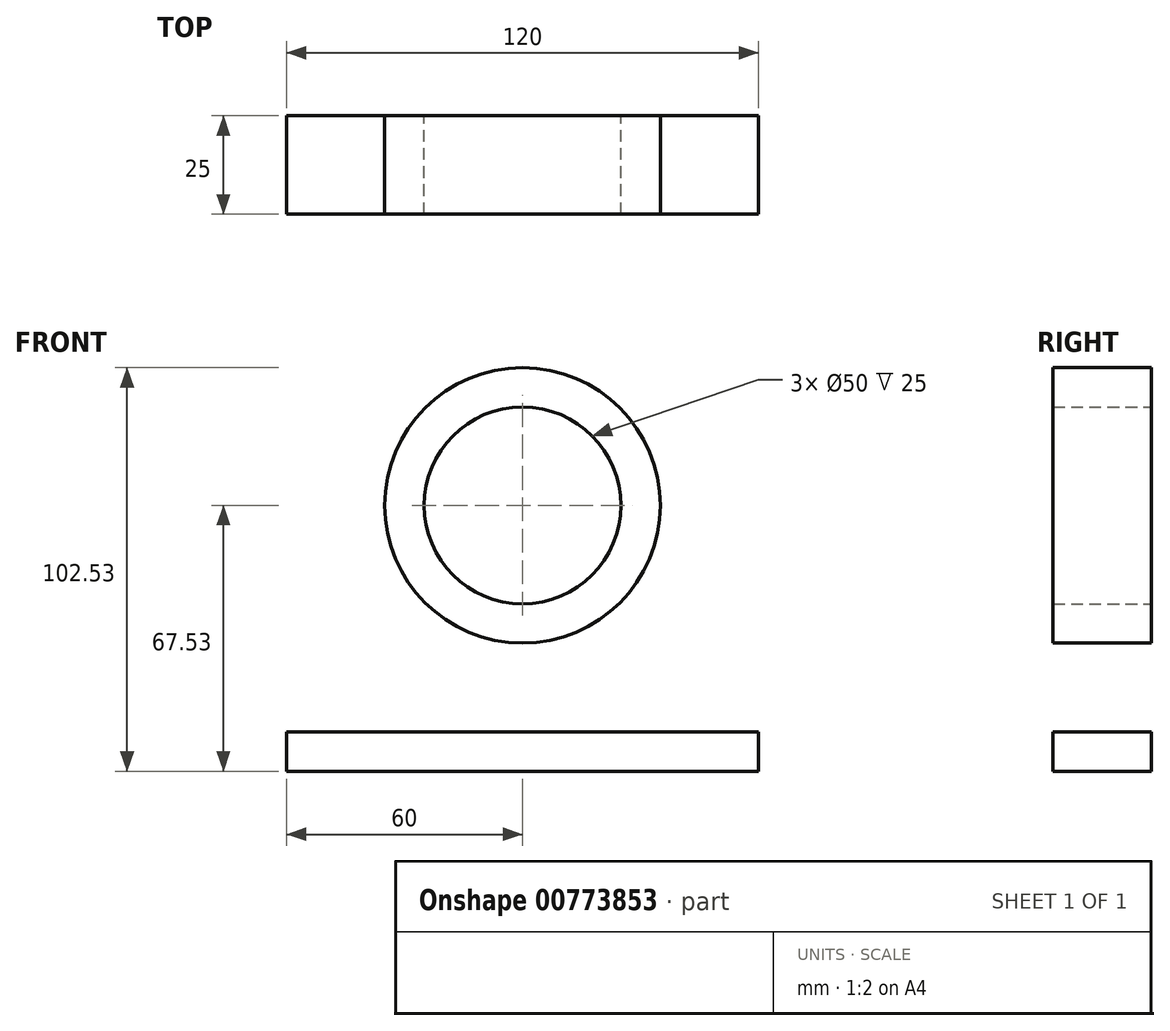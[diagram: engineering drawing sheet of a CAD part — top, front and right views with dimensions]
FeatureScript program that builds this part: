
annotation { "Feature Type Name" : "Feature", "Feature Type Description" : "" }
export const myFeature = defineFeature(function(context is Context, id is Id, definition is map)
    precondition{}
    {
        {
            var Q0;
            Q0=qCreatedBy(makeId("Front.planeOp"),FACE);
            var sketch = newSketch(context, id + "F0", { "sketchPlane" : qUnion([Q0])});
            skCircle(sketch, "E0", {"center": v(0, 0) * mm, "radius": 25 * mm});
            skCircle(sketch, "E1", {"center": v(0, 0) * mm, "radius": 35 * mm});
            skLineSegment(sketch, "E2", {"start": v(-60, -57.53) * mm, "end": v(60, -57.53) * mm});
            skLineSegment(sketch, "E3", {"start": v(-60, -57.53) * mm, "end": v(-60, -67.53) * mm});
            skLineSegment(sketch, "E4", {"start": v(-60, -67.53) * mm, "end": v(60, -67.53) * mm});
            skLineSegment(sketch, "E5", {"start": v(60, -67.53) * mm, "end": v(60, -57.53) * mm});
            skLineSegment(sketch, "E6", {"start": v(-32.7, 12.47) * mm, "end": v(-60, -57.53) * mm});
            skLineSegment(sketch, "E7", {"start": v(32.7, 12.47) * mm, "end": v(60, -57.53) * mm});
            skSolve(sketch);
        }
        {
            var Q0;
            Q0=makeQuery(id+"F0.imprint","IMPRINT",FACE,{"disambiguationData":[TD([[makeQuery(id+"F0.imprint","IMPRINT",EDGE,{"derivedFrom":sQuery(id+"F0.wireOp",EDGE,"E0")}),-1.0]])]});
            var Q1;
            {var subQ0=sQuery(id+"F0.wireOp",EDGE,"dgtYimct-kxXs-OjcF-jErT-LlOqedGBojv1");Q1=makeQuery(id+"F0.imprint","IMPRINT",FACE,{"disambiguationData":[TD([[makeQuery(id+"F0.imprint","IMPRINT",EDGE,{"derivedFrom":subQ0}),1.0]])]});}
            var Q2;
            Q2=makeQuery(id+"F0.imprint","IMPRINT",FACE,{"disambiguationData":[TD([[makeQuery(id+"F0.imprint","IMPRINT",EDGE,{"derivedFrom":sQuery(id+"F0.wireOp",EDGE,"E2")}),-1.0]])]});
            extrude(context, id + "F1", {"entities" : qUnion([Q0, Q1, Q2]), "endBound" : BoundingType.SYMMETRIC, "depth" : 25 * mm, "offsetDistance" : 25 * mm});
        }
    });
